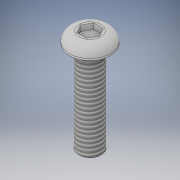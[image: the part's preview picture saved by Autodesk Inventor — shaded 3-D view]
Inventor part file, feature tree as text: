
AUTODESK INVENTOR PART (.ipt)
format: ipt  version: 2018 (Build 220112000, 112)  size: 137,728 bytes
history: native  units: in
note: dims shown in document units (in); Inventor stores cm internally (conversion verified against a paired STEP export)
features: extrude x3, sketch x3, fillet x1, thread x1, chamfer x1
ambient origin geometry x8: Origin, YZ Plane, XZ Plane, XY Plane, X Axis, Y Axis, Z Axis, Center Point
bodies: Solid1 (feature_tree)
feature tree (9):
  extrude  "Extrusion1"  Depth=0.0787in TaperAngle=0.0deg
  extrude  "Extrusion2"  Depth=0.0669in
  fillet  "Fillet1"  Radius=0.1575in
  extrude  "Extrusion3"  Depth=0.3937in TaperAngle=0.0deg
  thread  "Thread1"  [1 undecoded]
  chamfer  "Chamfer1"  [1 undecoded]
  sketch  "Sketch1"  dims[d0=0.2835in d1=0.0787in d2=0.0in]
  sketch  "Sketch2"  dims[d3=0.0394in d4=0.0in d5=0.0669in d6=0.1575in]
  sketch  "Sketch3"  dims[d7=0.6299in d8=0.0in d9=0.3937in d10=0.0in d11=0.0079in d12=0.0787in d13=45.0deg]
note: 2 required parameter values undecoded (feature->parameter linkage not recoverable at this tier; creation-order binding heuristic only, values carry confidence <= 0.55)
